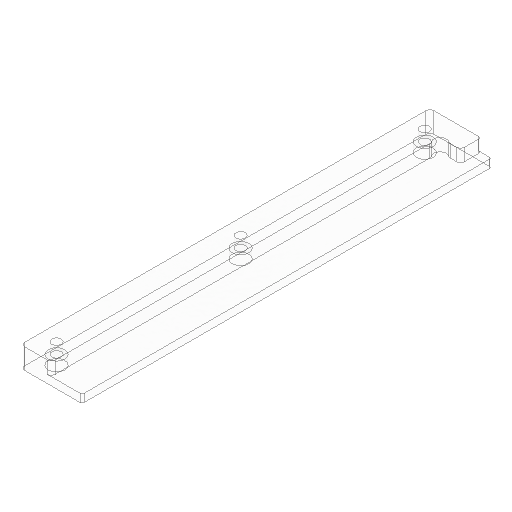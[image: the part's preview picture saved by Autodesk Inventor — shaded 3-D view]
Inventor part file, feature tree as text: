
AUTODESK INVENTOR PART (.ipt)
format: ipt  version: 2025.2 (Build 292293000, 293)  size: 160,768 bytes
history: native  units: in
note: dims shown in document units (in); Inventor stores cm internally (conversion verified against a paired STEP export)
features: sketch x2, extrude x2, hole x1, fillet x1, projected_geometry x1
ambient origin geometry x8: Origin, YZ Plane, XZ Plane, XY Plane, X Axis, Y Axis, Z Axis, Center Point
bodies: Solid1 (feature_tree)
feature tree (7):
  sketch  "Sketch1"  dims[d0=1.1811in d1=7.874in]
  extrude  "Extrusion1"  Depth=7.874in
  extrude  "Extrusion2"  Depth=0.5945in
  hole  "Hole1"  [1 undecoded]
  fillet  "Fillet1"  Radius=0.2402in
  sketch  "Sketch2"  dims[d2=0.3917in d3=0.5945in d4=0.3937in d5=0.0in d6=0.2402in d7=0.0in d8=7.0866in d9=0.1772in d10=0.2362in d11=0.315in d12=0.1811in d13=90.0deg d14=0.315in d15=0.8108in d16=0.0787in d17=0.2362in d18=0.0787in d22=0.0787in d23=0.5866in d24=0.0394in d25=0.2953in d27=0.3937in]
  projected_geometry  "Projected Loop1"
note: 1 required parameter value undecoded (feature->parameter linkage not recoverable at this tier; creation-order binding heuristic only, values carry confidence <= 0.55)
